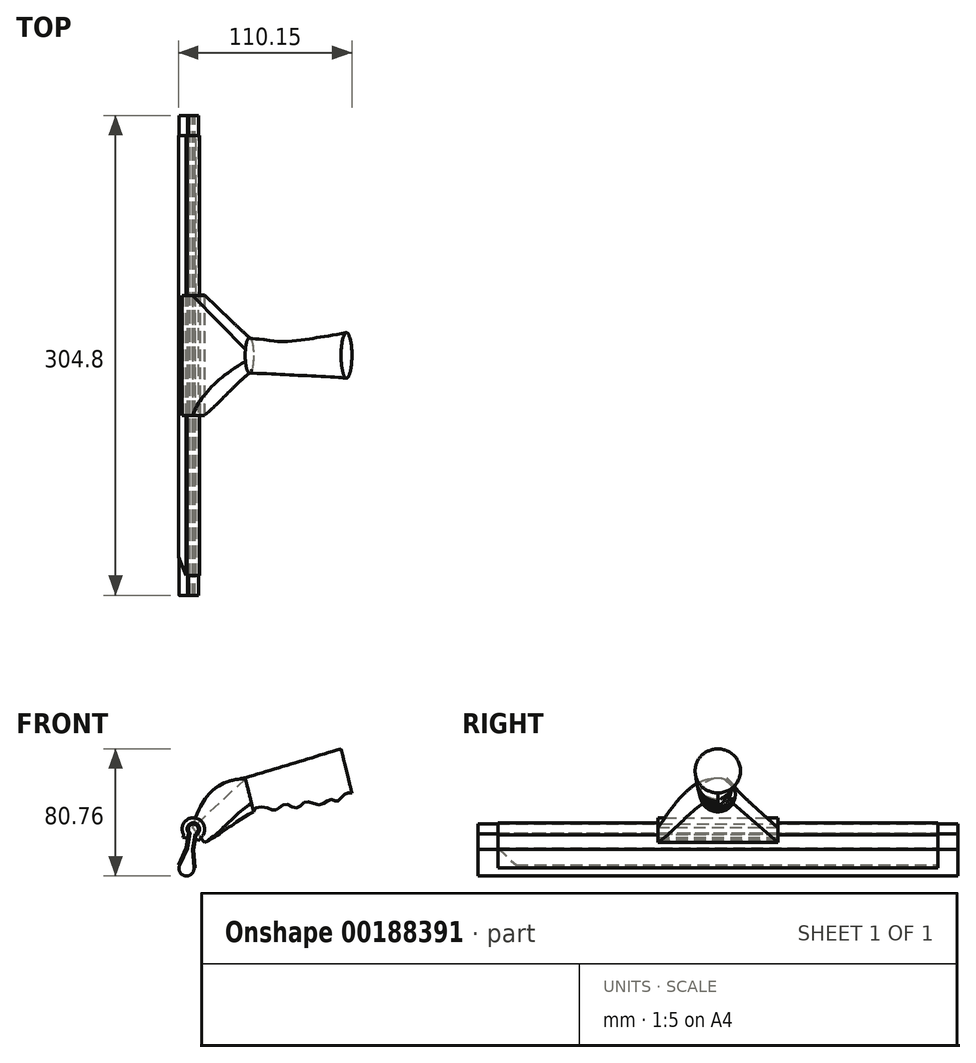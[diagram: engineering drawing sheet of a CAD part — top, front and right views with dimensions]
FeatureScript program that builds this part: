
annotation { "Feature Type Name" : "Feature", "Feature Type Description" : "" }
export const myFeature = defineFeature(function(context is Context, id is Id, definition is map)
    precondition{}
    {
        {
            var Q0;
            Q0=qCreatedBy(makeId("Front.planeOp"),FACE);
            var sketch = newSketch(context, id + "F0", { "sketchPlane" : qUnion([Q0])});
            skCircle(sketch, "E0", {"center": v(0, 0) * mm, "radius": 3.18 * mm});
            skCircle(sketch, "E1", {"center": v(-25.4, 0) * mm, "radius": 4.76 * mm});
            skLineSegment(sketch, "E2", {"start": v(-2.76, 1.57) * mm, "end": v(-12.7, 1.57) * mm});
            skLineSegment(sketch, "E3", {"start": v(-12.7, 1.57) * mm, "end": v(-24.19, 4.6) * mm});
            skLineSegment(sketch, "E4.MirrorCS", {"start": v(-2.76, -1.57) * mm, "end": v(-12.7, -1.57) * mm});
            skLineSegment(sketch, "E5.MirrorCS", {"start": v(-12.7, -1.57) * mm, "end": v(-24.19, -4.6) * mm});
            skSolve(sketch);
        }
        {
            var Q0;
            Q0=qSketchRegion(id+"F0",true);
            extrude(context, id + "F1", {"entities" : qUnion([Q0]), "depth" : 304.8 * mm, "symmetric" : true});
        }
        {
            var Q0;
            Q0=qCreatedBy(makeId("Front.planeOp"),FACE);
            var sketch = newSketch(context, id + "F2", { "sketchPlane" : qUnion([Q0])});
            skLineSegment(sketch, "E6.0", {"start": v(-12.7, 1.57) * mm, "end": v(-24.19, 4.6) * mm});
            skLineSegment(sketch, "E7.0", {"start": v(-2.76, 1.57) * mm, "end": v(-12.7, 1.57) * mm});
            skArc(sketch, "E8.0", {"start": v(-2.76, -1.57) * mm, "mid": v(3.18, 0) * mm, "end": v(-2.76, 1.57) * mm});
            skLineSegment(sketch, "E9.0", {"start": v(-2.76, -1.57) * mm, "end": v(-12.7, -1.57) * mm});
            skLineSegment(sketch, "E10.0", {"start": v(-12.7, -1.57) * mm, "end": v(-24.19, -4.6) * mm});
            skLineSegment(sketch, "E11.0", {"start": v(-12.6, 2.39) * mm, "end": v(-23.98, 5.4) * mm});
            skLineSegment(sketch, "E11.1", {"start": v(-12.6, -2.39) * mm, "end": v(-23.98, -5.4) * mm});
            skLineSegment(sketch, "E11.2", {"start": v(-3.2, -2.39) * mm, "end": v(-12.6, -2.39) * mm});
            skArc(sketch, "E11.3", {"start": v(-3.2, -2.39) * mm, "mid": v(3.99, 0) * mm, "end": v(-3.2, 2.39) * mm});
            skLineSegment(sketch, "E11.4", {"start": v(-3.2, 2.39) * mm, "end": v(-12.6, 2.39) * mm});
            skLineSegment(sketch, "E12", {"start": v(-24.19, 4.6) * mm, "end": v(-23.98, 5.4) * mm});
            skLineSegment(sketch, "E13", {"start": v(-23.98, -5.4) * mm, "end": v(-24.19, -4.6) * mm});
            skSolve(sketch);
        }
        {
            var Q0;
            Q0=makeQuery(id+"F2.imprint","IMPRINT",FACE,{"disambiguationData":[TD([[makeQuery(id+"F2.imprint","IMPRINT",EDGE,{"derivedFrom":sQuery(id+"F2.wireOp",EDGE,"E6.0")}),-1.0]])]});
            extrude(context, id + "F3", {"entities" : qUnion([Q0]), "depth" : 279.4 * mm, "symmetric" : true});
        }
        {
            var Q0;
            Q0=makeQuery(id+"F3.opExtrude","SWEPT_FACE",FACE,{"disambiguationData":[OSD([sQuery(id+"F2.wireOp",EDGE,"E11.0")])]});
            var sketch = newSketch(context, id + "F4", { "sketchPlane" : qUnion([Q0])});
            skLineSegment(sketch, "E14", {"start": v(-12.79, -139.7) * mm, "end": v(-24.56, -127.93) * mm});
            skLineSegment(sketch, "E15", {"start": v(-24.56, -127.93) * mm, "end": v(-24.56, -139.7) * mm});
            skLineSegment(sketch, "E16", {"start": v(-24.56, -139.7) * mm, "end": v(-12.79, -139.7) * mm});
            skSolve(sketch);
        }
        {
            var Q0;
            Q0=makeQuery(id+"F4.imprint","IMPRINT",FACE,{"disambiguationData":[TD([[makeQuery(id+"F4.imprint","IMPRINT",EDGE,{"derivedFrom":sQuery(id+"F4.wireOp",EDGE,"E14")}),1.0]])]});
            extrude(context, id + "F5", {"entities" : qUnion([Q0]), "operationType" : NewBodyOperationType.REMOVE, "oppositeDirection" : true, "depth" : 0.81 * mm});
        }
        {
            var Q0;
            Q0=qCreatedBy(makeId("Front.planeOp"),FACE);
            var sketch = newSketch(context, id + "F6", { "sketchPlane" : qUnion([Q0])});
            skArc(sketch, "E17.0", {"start": v(-3.2, -2.39) * mm, "mid": v(3.99, 0) * mm, "end": v(-3.2, 2.39) * mm});
            skLineSegment(sketch, "E18.0", {"start": v(-3.2, 2.39) * mm, "end": v(-6.35, 2.39) * mm});
            skLineSegment(sketch, "E19.0", {"start": v(-3.2, -2.39) * mm, "end": v(-6.35, -2.39) * mm});
            skLineSegment(sketch, "E20.0", {"start": v(-4.51, 5.56) * mm, "end": v(-6.35, 5.56) * mm});
            skArc(sketch, "E20.1", {"start": v(-4.51, -5.56) * mm, "mid": v(7.16, 0) * mm, "end": v(-4.51, 5.56) * mm});
            skLineSegment(sketch, "E20.2", {"start": v(-4.51, -5.56) * mm, "end": v(-6.35, -5.56) * mm});
            skLineSegment(sketch, "E21", {"start": v(-6.35, 2.39) * mm, "end": v(-6.35, 5.56) * mm});
            skLineSegment(sketch, "E22", {"start": v(-6.35, -2.39) * mm, "end": v(-6.35, -5.56) * mm});
            skPoint(sketch, "E23.orphan", {"position": v(-12.6, -2.39) * mm});
            skPoint(sketch, "E24.orphan", {"position": v(-12.6, 2.39) * mm});
            skSolve(sketch);
        }
        {
            var Q0;
            Q0=qSketchRegion(id+"F6",true);
            extrude(context, id + "F7", {"entities" : qUnion([Q0]), "operationType" : NewBodyOperationType.ADD, "depth" : 76.2 * mm, "symmetric" : true});
        }
        {
            var Q0;
            Q0=qCreatedBy(makeId("Front.planeOp"),FACE);
            var sketch = newSketch(context, id + "F8", { "sketchPlane" : qUnion([Q0])});
            skLineSegment(sketch, "E25", {"start": v(31.4, 38.8) * mm, "end": v(43.22, -9.26) * mm, "construction": true});
            skSolve(sketch);
        }
        {
            var Q0;
            Q0=qCreatedBy(makeId("Right.planeOp"),FACE);
            var Q1;
            Q1=sQuery(id+"F8.wireOp",EDGE,"E25");
            cPlane(context, id + "F9", {"entities" : qUnion([Q0, Q1]), "cplaneType" : CPlaneType.LINE_ANGLE, "offset" : 25.4 * mm, "angle" : 0 * degree, "width" : 152.4 * mm, "height" : 152.4 * mm});
        }
        {
            var Q0;
            Q0=qCreatedBy(id+"F9.planeOp",FACE);
            cPlane(context, id + "F10", {"entities" : qUnion([Q0]), "cplaneType" : CPlaneType.OFFSET, "offset" : 63.5 * mm, "oppositeDirection" : true, "width" : 152.4 * mm, "height" : 152.4 * mm});
        }
        {
            var Q0;
            Q0=qCreatedBy(id+"F9.planeOp",FACE);
            var sketch = newSketch(context, id + "F11", { "sketchPlane" : qUnion([Q0])});
            skPoint(sketch, "E26", {"position": v(0, 23.81) * mm});
            skPoint(sketch, "E27", {"position": v(0, 1.59) * mm});
            skLineSegment(sketch, "E28", {"start": v(0, 12.7) * mm, "end": v(-3.8, 23.14) * mm, "construction": true});
            skLineSegment(sketch, "E29", {"start": v(0, 12.7) * mm, "end": v(3.8, 23.14) * mm, "construction": true});
            skLineSegment(sketch, "E30", {"start": v(0, 12.7) * mm, "end": v(0, 23.81) * mm, "construction": true});
            skLineSegment(sketch, "E31", {"start": v(0, 12.7) * mm, "end": v(-9.62, 7.14) * mm, "construction": true});
            skLineSegment(sketch, "E32", {"start": v(0, 12.7) * mm, "end": v(9.62, 7.14) * mm, "construction": true});
            skArc(sketch, "E33", {"start": v(-3.8, 23.14) * mm, "mid": v(-10.44, 16.5) * mm, "end": v(-9.62, 7.14) * mm});
            skArc(sketch, "E34", {"start": v(3.8, 23.14) * mm, "mid": v(0, 23.81) * mm, "end": v(-3.8, 23.14) * mm});
            skArc(sketch, "E35", {"start": v(9.62, 7.14) * mm, "mid": v(10.44, 16.5) * mm, "end": v(3.8, 23.14) * mm});
            skArc(sketch, "E36", {"start": v(-9.62, 7.14) * mm, "mid": v(0, 1.59) * mm, "end": v(9.62, 7.14) * mm});
            skSolve(sketch);
        }
        {
            var Q0;
            Q0=qCreatedBy(id+"F10.planeOp",FACE);
            var sketch = newSketch(context, id + "F12", { "sketchPlane" : qUnion([Q0])});
            skPoint(sketch, "E37", {"position": v(0, 27.11) * mm});
            skPoint(sketch, "E38", {"position": v(0, -1.71) * mm});
            skArc(sketch, "E39", {"start": v(0, 27.11) * mm, "mid": v(-14.41, 12.74) * mm, "end": v(-0.08, -1.71) * mm});
            skArc(sketch, "E40", {"start": v(-0.08, -1.71) * mm, "mid": v(14.41, 12.66) * mm, "end": v(0, 27.11) * mm});
            skSolve(sketch);
        }
        {
            var Q0;
            Q0=qCreatedBy(makeId("Front.planeOp"),FACE);
            var sketch = newSketch(context, id + "F13", { "sketchPlane" : qUnion([Q0])});
            skLineSegment(sketch, "E41", {"start": v(32.93, 32.62) * mm, "end": v(93.8, 50.98) * mm});
            skFitSpline(sketch, "E42", {"points": [v(38.23, 11.03) * mm, v(45.88, 13.7) * mm, v(52.41, 12.07) * mm, v(58.12, 15.79) * mm, v(65.72, 13.54) * mm, v(71.42, 17.34) * mm, v(80.4, 15.44) * mm, v(87.14, 18.8) * mm, v(91.46, 17.6) * mm, v(95.96, 22) * mm, v(100.68, 22.98) * mm], "startDerivative": vector(-19.35, 78.7) * mm, "endDerivative": vector(58.24, -1.55) * mm});
            skLineSegment(sketch, "E43", {"start": v(33.86, 9.96) * mm, "end": v(38.23, 11.03) * mm, "construction": true});
            skSolve(sketch);
        }
        {
            var Q0;
            Q0=makeQuery(id+"F12.imprint","IMPRINT",FACE,{"disambiguationData":[TD([[makeQuery(id+"F12.imprint","IMPRINT",EDGE,{"derivedFrom":sQuery(id+"F12.wireOp",EDGE,"E39")}),1.0]])]});
            var Q1;
            Q1=makeQuery(id+"F11.imprint","IMPRINT",FACE,{"disambiguationData":[TD([[makeQuery(id+"F11.imprint","IMPRINT",EDGE,{"derivedFrom":sQuery(id+"F11.wireOp",EDGE,"E33")}),1.0]])]});
            var Q2;
            Q2=sQuery(id+"F13.wireOp",EDGE,"E42");
            var Q3;
            Q3=sQuery(id+"F13.wireOp",EDGE,"E41");
            loft(context, id + "F14", {"addGuides" : true, "sheetProfilesArray" : [{ "sheetProfileEntities" : qUnion([Q0]) }, { "sheetProfileEntities" : qUnion([Q1]) }], "guidesArray" : [{ "guideEntities" : qUnion([Q2]), "guideDerivativeType" : LoftGuideDerivativeType.DEFAULT, "guideDerivativeMagnitude" : 1 }, { "guideEntities" : qUnion([Q3]), "guideDerivativeType" : LoftGuideDerivativeType.DEFAULT, "guideDerivativeMagnitude" : 1 }]});
        }
        {
            var Q0;
            Q0=makeQuery(id+"F3.opExtrude","SWEPT_BODY",BODY,{"disambiguationData":[OSD([sQuery(id+"F2.wireOp",EDGE,"E6.0"),sQuery(id+"F2.wireOp",EDGE,"E7.0"),sQuery(id+"F2.wireOp",EDGE,"E8.0"),sQuery(id+"F2.wireOp",EDGE,"E9.0"),sQuery(id+"F2.wireOp",EDGE,"E10.0"),sQuery(id+"F2.wireOp",EDGE,"E11.0"),sQuery(id+"F2.wireOp",EDGE,"E11.1"),sQuery(id+"F2.wireOp",EDGE,"E11.2"),sQuery(id+"F2.wireOp",EDGE,"E11.3"),sQuery(id+"F2.wireOp",EDGE,"E11.4"),sQuery(id+"F2.wireOp",EDGE,"E12"),sQuery(id+"F2.wireOp",EDGE,"E13")])]});
            var Q1;
            Q1=makeQuery(id+"F1.opExtrude","SWEPT_BODY",BODY,{"disambiguationData":[OSD([sQuery(id+"F0.wireOp",EDGE,"E0"),sQuery(id+"F0.wireOp",EDGE,"E1"),sQuery(id+"F0.wireOp",EDGE,"E2"),sQuery(id+"F0.wireOp",EDGE,"E3"),sQuery(id+"F0.wireOp",EDGE,"E4.MirrorCS"),sQuery(id+"F0.wireOp",EDGE,"E5.MirrorCS")])]});
            var Q2;
            Q2=makeQuery(id+"F1.opExtrude","SWEPT_FACE",FACE,{"disambiguationData":[OSD([sQuery(id+"F0.wireOp",EDGE,"E0")])]});
            transform(context, id + "F15", {"entities" : qUnion([Q0, Q1]), "transformType" : TransformType.ROTATION, "transformAxis" : qUnion([Q2]), "angle" : 30 * degree, "oppositeDirection" : true, "makeCopy" : false});
        }
        {
            var Q0;
            Q0=makeQuery(id+"F3.opExtrude","SWEPT_BODY",BODY,{"disambiguationData":[OSD([sQuery(id+"F2.wireOp",EDGE,"E6.0"),sQuery(id+"F2.wireOp",EDGE,"E7.0"),sQuery(id+"F2.wireOp",EDGE,"E8.0"),sQuery(id+"F2.wireOp",EDGE,"E9.0"),sQuery(id+"F2.wireOp",EDGE,"E10.0"),sQuery(id+"F2.wireOp",EDGE,"E11.0"),sQuery(id+"F2.wireOp",EDGE,"E11.1"),sQuery(id+"F2.wireOp",EDGE,"E11.2"),sQuery(id+"F2.wireOp",EDGE,"E11.3"),sQuery(id+"F2.wireOp",EDGE,"E11.4"),sQuery(id+"F2.wireOp",EDGE,"E12"),sQuery(id+"F2.wireOp",EDGE,"E13")])]});
            var Q1;
            Q1=makeQuery(id+"F1.opExtrude","SWEPT_BODY",BODY,{"disambiguationData":[OSD([sQuery(id+"F0.wireOp",EDGE,"E0"),sQuery(id+"F0.wireOp",EDGE,"E1"),sQuery(id+"F0.wireOp",EDGE,"E2"),sQuery(id+"F0.wireOp",EDGE,"E3"),sQuery(id+"F0.wireOp",EDGE,"E4.MirrorCS"),sQuery(id+"F0.wireOp",EDGE,"E5.MirrorCS")])]});
            var Q2;
            {var subQ1=sQuery(id+"F2.wireOp",EDGE,"E11.3");Q2=makeQuery(id+"F7.boolean.opBoolean","SPLIT",FACE,{"disambiguationData":[TD([makeQuery(id+"F7.opExtrude","CAP_FACE",FACE,{"disambiguationData":[OSD([sQuery(id+"F6.wireOp",EDGE,"E17.0"),sQuery(id+"F6.wireOp",EDGE,"E18.0"),sQuery(id+"F6.wireOp",EDGE,"E19.0"),sQuery(id+"F6.wireOp",EDGE,"E20.0"),sQuery(id+"F6.wireOp",EDGE,"E20.1"),sQuery(id+"F6.wireOp",EDGE,"E20.2"),sQuery(id+"F6.wireOp",EDGE,"E21"),sQuery(id+"F6.wireOp",EDGE,"E22")])],"isStart":false})])],"derivedFrom":makeQuery(id+"F3.opExtrude","SWEPT_FACE",FACE,{"disambiguationData":[OSD([subQ1])]})});}
            transform(context, id + "F16", {"entities" : qUnion([Q0, Q1]), "transformType" : TransformType.ROTATION, "transformAxis" : qUnion([Q2]), "angle" : 310 * degree, "makeCopy" : false});
        }
        {
            var Q0;
            Q0=qCreatedBy(makeId("Right.planeOp"),FACE);
            var Q1;
            {var subQ1=sQuery(id+"F2.wireOp",EDGE,"E11.3");Q1=makeQuery(id+"F7.boolean.opBoolean","SPLIT",FACE,{"disambiguationData":[TD([makeQuery(id+"F7.opExtrude","CAP_FACE",FACE,{"disambiguationData":[OSD([sQuery(id+"F6.wireOp",EDGE,"E17.0"),sQuery(id+"F6.wireOp",EDGE,"E18.0"),sQuery(id+"F6.wireOp",EDGE,"E19.0"),sQuery(id+"F6.wireOp",EDGE,"E20.0"),sQuery(id+"F6.wireOp",EDGE,"E20.1"),sQuery(id+"F6.wireOp",EDGE,"E20.2"),sQuery(id+"F6.wireOp",EDGE,"E21"),sQuery(id+"F6.wireOp",EDGE,"E22")])],"isStart":false})])],"derivedFrom":makeQuery(id+"F3.opExtrude","SWEPT_FACE",FACE,{"disambiguationData":[OSD([subQ1])]})});}
            cPlane(context, id + "F17", {"entities" : qUnion([Q0, Q1]), "cplaneType" : CPlaneType.LINE_ANGLE, "offset" : 25.4 * mm, "angle" : 320 * degree, "width" : 152.4 * mm, "height" : 152.4 * mm});
        }
        {
            var Q0;
            Q0=qCreatedBy(id+"F17.planeOp",FACE);
            var sketch = newSketch(context, id + "F18", { "sketchPlane" : qUnion([Q0])});
            skLineSegment(sketch, "E44.bottom", {"start": v(-38.26, 0.87) * mm, "end": v(37.94, 0.87) * mm});
            skLineSegment(sketch, "E44.top", {"start": v(-38.26, -11.2) * mm, "end": v(37.94, -11.2) * mm});
            skLineSegment(sketch, "E44.left", {"start": v(-38.26, 0.87) * mm, "end": v(-38.26, -11.2) * mm});
            skLineSegment(sketch, "E44.right", {"start": v(37.94, 0.87) * mm, "end": v(37.94, -11.2) * mm});
            skSolve(sketch);
        }
        {
            var Q0;
            Q0=sQuery(id+"F18.wireOp",VERTEX,"E44.right.start");
            var Q1;
            Q1=sQuery(id+"F18.wireOp",VERTEX,"E44.right.end");
            var Q2;
            Q2=sQuery(id+"F11.wireOp",VERTEX,"E34.start");
            cPlane(context, id + "F19", {"entities" : qUnion([Q0, Q1, Q2]), "cplaneType" : CPlaneType.THREE_POINT, "offset" : 25.4 * mm, "width" : 152.4 * mm, "height" : 152.4 * mm});
        }
        {
            var Q0;
            Q0=qCreatedBy(id+"F19.planeOp",FACE);
            var sketch = newSketch(context, id + "F20", { "sketchPlane" : qUnion([Q0])});
            skFitSpline(sketch, "E45", {"points": [v(16.28, -15.76) * mm, v(-21.56, 27.2) * mm], "startDerivative": vector(-16.36, 65.27) * mm, "endDerivative": vector(-64.67, 14.4) * mm});
            skSolve(sketch);
        }
        {
            var Q0;
            Q0=sQuery(id+"F18.wireOp",VERTEX,"E44.right.end");
            var Q1;
            Q1=sQuery(id+"F20.wireOp",VERTEX,"E45.0.internal");
            var Q2;
            Q2=sQuery(id+"F11.wireOp",VERTEX,"E36.end");
            cPlane(context, id + "F21", {"entities" : qUnion([Q0, Q1, Q2]), "cplaneType" : CPlaneType.THREE_POINT, "offset" : 25.4 * mm, "width" : 152.4 * mm, "height" : 152.4 * mm});
        }
        {
            var Q0;
            Q0=qCreatedBy(id+"F21.planeOp",FACE);
            var sketch = newSketch(context, id + "F22", { "sketchPlane" : qUnion([Q0])});
            skFitSpline(sketch, "E46", {"points": [v(-7.44, -23.86) * mm, v(25.85, 10.8) * mm], "startDerivative": vector(37.21, 31.11) * mm, "endDerivative": vector(37.21, 31.11) * mm});
            skSolve(sketch);
        }
        {
            var Q0;
            Q0=makeQuery(id+"F11.imprint","IMPRINT",FACE,{"disambiguationData":[TD([[makeQuery(id+"F11.imprint","IMPRINT",EDGE,{"derivedFrom":sQuery(id+"F11.wireOp",EDGE,"E33")}),1.0]])]});
            var Q1;
            Q1=qSketchRegion(id+"F18",true);
            var Q2;
            Q2=makeQuery(id+"F5Hj00Dxn6HWM3p_4.opPattern","COPY",EDGE,{"derivedFrom":makeQuery(id+"FHdUuU8fxAqwqxB_3.opExtrude","CAP_EDGE",EDGE,{"disambiguationData":[OSD([sQuery(id+"F20.wireOp",EDGE,"E45")])],"isStart":true}),"instanceName":"1"});
            var Q3;
            Q3=sQuery(id+"F20.wireOp",EDGE,"E45");
            var Q4;
            Q4=qConstructionFilter(qBodyType(qCreatedBy(id+"F22",EDGE),BodyType.WIRE),ConstructionObject.NO);
            loft(context, id + "F23", {"addGuides" : true, "sheetProfilesArray" : [{ "sheetProfileEntities" : qUnion([Q0]) }, { "sheetProfileEntities" : qUnion([Q1]) }], "guidesArray" : [{ "guideEntities" : qUnion([Q2]), "guideDerivativeType" : LoftGuideDerivativeType.DEFAULT, "guideDerivativeMagnitude" : 1 }, { "guideEntities" : qUnion([Q3]), "guideDerivativeType" : LoftGuideDerivativeType.DEFAULT, "guideDerivativeMagnitude" : 1 }, { "guideEntities" : qUnion([Q4]), "guideDerivativeType" : LoftGuideDerivativeType.DEFAULT, "guideDerivativeMagnitude" : 1 }]});
        }
    });
